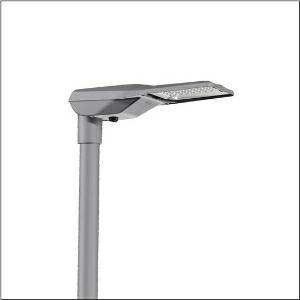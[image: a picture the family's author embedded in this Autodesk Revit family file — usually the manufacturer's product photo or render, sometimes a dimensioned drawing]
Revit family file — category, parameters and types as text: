
# Revit family: streetlight_sl_21_mini___p0_5a_5xe2v33r08hb_69df
name_source: partatom
category: Lighting Fixtures
units: mm (PartAtom-declared; Revit-internal decimal feet)

## family parameters
Cut with Voids When Loaded = No
Host = Face
Light Source = No
Part Type = Normal
Room Calculation Point = No
Round Connector Dimension = Use Diameter
Shared = No

## types (1)
- --- (1 x LED, 8890 lm, 66 W, 3000K)
    Apparent Load = 66 VA
    CIE Flux Codes = 37 73 96 100 100
    Color Rendering = 70
    Color Temperature = 3000K
    Default Elevation = 1800 mm
    Description = Streetlight SL 21 mini, mast luminaire, primary light control with lens, of PMMA, primary optical cover: cover, of toughened safety glass, transparent, light distribution: P0.5a, light emission: direct distribution, primary light characteristic: asymmetric, installation type: post-top, side-entry, LED, High Power LED, rated luminous flux: 8.890lm, luminous efficacy: 135lm/W, light colour: 730, colour temperature: 3000K, control gear: D4i, control: pre-setting: logarithmic dimming characteristic, flexible luminous flux parameterisation, time-dependent luminous flux control, constant luminous flux control, overheat protection, mains connection: 220..240V, AC, 50/60Hz, start of lifetime: 66W, end of service life: 69W, reduction: 30W, luminaire housing, of diecast aluminium, powder-coated, SITECO metallic grey (DB 702S), corrosivity category C5 high according to DIN EN ISO 12944, multi-level sealing system, sealing non-destructively replaceable, inclination adjustable: 0°, 5°, 10°, 15°, please order mast flange separately, length: 628mm, width: 235mm, height: 110mm, mast flange for spigot size: 42mm (side-entry): 5XC10008XM4, 60/48mm (side-entry/post-top): 5XC10108XM2, 76/60mm (side-entry/post-top): 5XC10108XM1, mounting height: 4..8m, Smart Interface below, protection rating (complete): IP66, insulation class (complete): insulation class II (safety insulation), certification: CE, ENEC, ENEC+, VDE, impact resistance: IK10, permissible operating ambient temperature for outdoor applications: -40..+50°C, standard-compliant lighting for roads and squares, packaging unit: 1 piece

Light Distribution: P0.5a
    Height = 110 mm
    Lamp = 1 x LED
    Lamp Light Flux = 8890 lm
    Lamp Power = 66 W
    Lamp count = 1
    Length = 625 mm
    Luminous efficacy = 135 lm/W
    Manufacturer = Siteco
    ModVariant = No
    Model = 5XE2V33R08HB
    Number of Poles = 1
    OnlyDefault = Yes
    Power Factor = 1
    Product Name = Streetlight SL 21 mini | P0.5a
    Product group = mast luminaire | pylon top
    ProductGroupID = 6100
    Protection Class = Protection class II
    Protection Degree = IP 66
    RLX_Detail_Level = 1
    RLX_Emergency_Light_Flux = 0 lm
    RLX_Emergency_Type = 0
    RLX_Emergency_Type_DB = No
    RlxData = <blob elided: 93377 chars, md5=d44a001a>
    Socket = socket
    Standby Power = 0 W
    System Light Flux = 8890 lm
    System Power = 66 W
    Type Comments = factory setting: luminous flux: 100 % | dim-lin: 254 | 670 mA
    Type Image = l_1003516.jpg
    URL = http://relux.com
    VarID = @adj_077581
    Voltage = 0 V
    Weight = 0.00 kg
    Width = 234 mm

## geometry (parser evidence)
native form markers: Blend x4, Sweep x12
no freeform markers — native parametric forms only
